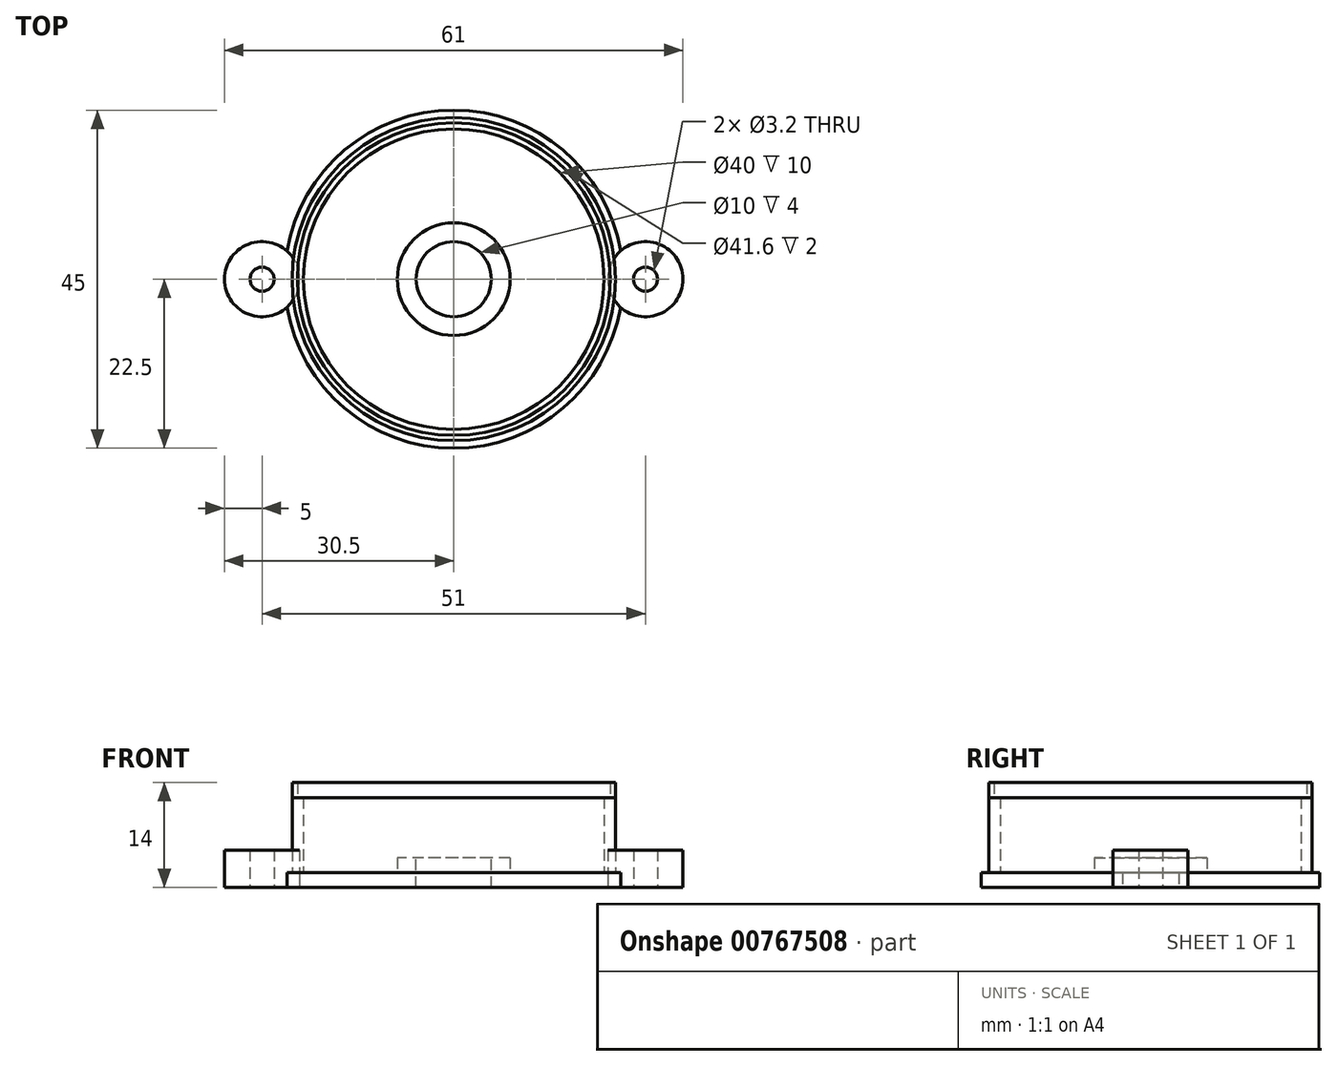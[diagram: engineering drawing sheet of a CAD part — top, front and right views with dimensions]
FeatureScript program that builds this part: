
annotation { "Feature Type Name" : "Feature", "Feature Type Description" : "" }
export const myFeature = defineFeature(function(context is Context, id is Id, definition is map)
    precondition{}
    {
        {
            var Q0;
            Q0=qCreatedBy(makeId("Top.planeOp"),FACE);
            var sketch = newSketch(context, id + "F0", { "sketchPlane" : qUnion([Q0])});
            skCircle(sketch, "E0", {"center": v(0, 0) * mm, "radius": 22.5 * mm});
            skCircle(sketch, "E1", {"center": v(25.5, 0) * mm, "radius": 5 * mm});
            skCircle(sketch, "E2", {"center": v(25.5, 0) * mm, "radius": 1.6 * mm});
            skCircle(sketch, "E3.1.0", {"center": v(-25.5, 0) * mm, "radius": 5 * mm});
            skCircle(sketch, "E3.1.1", {"center": v(-25.5, 0) * mm, "radius": 1.6 * mm});
            skSolve(sketch);
        }
        {
            var Q0;
            Q0=makeQuery(id+"F0.imprint","IMPRINT",FACE,{"disambiguationData":[TD([[makeQuery(id+"F0.imprint","IMPRINT",EDGE,{"derivedFrom":sQuery(id+"F0.wireOp",EDGE,"E3.1.1")}),-1.0]])]});
            var Q1;
            {var subQ0=sQuery(id+"F0.wireOp",EDGE,"E3.1.0");var subQ1=sQuery(id+"F0.wireOp",EDGE,"E0");var subQ2=makeQuery(id+"F0.imprint","INTERSECT",VERTEX,{"disambiguationData":[OD(0.0)],"derivedFrom":[subQ1,subQ0]});Q1=makeQuery(id+"F0.imprint","IMPRINT",FACE,{"disambiguationData":[TD([[makeQuery(id+"F0.imprint","IMPRINT",EDGE,{"disambiguationData":[TD([[subQ2,-1.0]])],"derivedFrom":subQ1}),1.0]])]});}
            var Q2;
            Q2=makeQuery(id+"F0.imprint","IMPRINT",FACE,{"disambiguationData":[TD([[makeQuery(id+"F0.imprint","IMPRINT",EDGE,{"derivedFrom":sQuery(id+"F0.wireOp",EDGE,"E2")}),-1.0]])]});
            var Q3;
            {var subQ0=sQuery(id+"F0.wireOp",EDGE,"E1");var subQ1=sQuery(id+"F0.wireOp",EDGE,"E0");var subQ2=makeQuery(id+"F0.imprint","INTERSECT",VERTEX,{"disambiguationData":[OD(0.0)],"derivedFrom":[subQ1,subQ0]});Q3=makeQuery(id+"F0.imprint","IMPRINT",FACE,{"disambiguationData":[TD([[makeQuery(id+"F0.imprint","IMPRINT",EDGE,{"disambiguationData":[TD([[subQ2,1.0]])],"derivedFrom":subQ1}),1.0]])]});}
            extrude(context, id + "F1", {"entities" : qUnion([Q0, Q1, Q2, Q3]), "depth" : 5 * mm, "offsetDistance" : 25 * mm});
        }
        {
            var Q0;
            {var subQ0=sQuery(id+"F0.wireOp",EDGE,"E3.1.0");var subQ1=sQuery(id+"F0.wireOp",EDGE,"E0");var subQ2=makeQuery(id+"F0.imprint","INTERSECT",VERTEX,{"disambiguationData":[OD(0.0)],"derivedFrom":[subQ1,subQ0]});Q0=makeQuery(id+"F0.imprint","IMPRINT",FACE,{"disambiguationData":[TD([[makeQuery(id+"F0.imprint","IMPRINT",EDGE,{"disambiguationData":[TD([[subQ2,1.0]])],"derivedFrom":subQ1}),1.0]])]});}
            extrude(context, id + "F2", {"entities" : qUnion([Q0]), "depth" : 2 * mm, "offsetDistance" : 25 * mm});
        }
        {
            var Q0;
            Q0=makeQuery(id+"F2.opExtrude","CAP_FACE",FACE,{"disambiguationData":[OSD([sQuery(id+"F0.wireOp",EDGE,"E0"),sQuery(id+"F0.wireOp",EDGE,"E1"),sQuery(id+"F0.wireOp",EDGE,"E3.1.0")])],"isStart":false});
            var sketch = newSketch(context, id + "F3", { "sketchPlane" : qUnion([Q0])});
            skCircle(sketch, "E4", {"center": v(0, 0) * mm, "radius": 20 * mm});
            skCircle(sketch, "E5", {"center": v(0, 0) * mm, "radius": 21.5 * mm});
            skSolve(sketch);
        }
        {
            var Q0;
            Q0=makeQuery(id+"F3.imprint","IMPRINT",FACE,{"disambiguationData":[TD([[makeQuery(id+"F3.imprint","IMPRINT",EDGE,{"derivedFrom":sQuery(id+"F3.wireOp",EDGE,"E4")}),-1.0]])]});
            var Q1;
            {var subQ1=makeQuery(id+"F2.opExtrude","CAP_EDGE",EDGE,{"disambiguationData":[OSD([sQuery(id+"F0.wireOp",EDGE,"E3.1.0")])],"isStart":false});Q1=makeQuery(id+"F3.imprint","IMPRINT",FACE,{"disambiguationData":[TD([[makeQuery(id+"F3.imprint","IMPRINT",EDGE,{"derivedFrom":subQ1}),1.0]])]});}
            var Q2;
            {var subQ1=makeQuery(id+"F2.opExtrude","CAP_EDGE",EDGE,{"disambiguationData":[OSD([sQuery(id+"F0.wireOp",EDGE,"E1")])],"isStart":false});Q2=makeQuery(id+"F3.imprint","IMPRINT",FACE,{"disambiguationData":[TD([[makeQuery(id+"F3.imprint","IMPRINT",EDGE,{"derivedFrom":subQ1}),1.0]])]});}
            extrude(context, id + "F4", {"entities" : qUnion([Q0, Q1, Q2]), "depth" : 10 * mm, "offsetDistance" : 25 * mm});
        }
        {
            var Q0;
            Q0=makeQuery(id+"F4.opExtrude","CAP_FACE",FACE,{"disambiguationData":[OSD([sQuery(id+"F3.wireOp",EDGE,"E4"),sQuery(id+"F3.wireOp",EDGE,"E5")])],"isStart":false});
            var sketch = newSketch(context, id + "F5", { "sketchPlane" : qUnion([Q0])});
            skCircle(sketch, "E6", {"center": v(0, 0) * mm, "radius": 20.8 * mm});
            skCircle(sketch, "E7", {"center": v(0, 0) * mm, "radius": 21.5 * mm});
            skSolve(sketch);
        }
        {
            var Q0;
            Q0=makeQuery(id+"F5.imprint","IMPRINT",FACE,{"disambiguationData":[TD([[makeQuery(id+"F5.imprint","IMPRINT",EDGE,{"derivedFrom":sQuery(id+"F5.wireOp",EDGE,"E6")}),-1.0]])]});
            extrude(context, id + "F6", {"entities" : qUnion([Q0]), "depth" : 2 * mm, "offsetDistance" : 25 * mm});
        }
        {
            var Q0;
            Q0=makeQuery(id+"FuXeZ9usWzECoiR_2.boolean.opBoolean","SPLIT",FACE,{"disambiguationData":[TD([makeQuery(id+"FuXeZ9usWzECoiR_2.opExtrude","SWEPT_FACE",FACE,{"disambiguationData":[OSD([sQuery(id+"F3.wireOp",EDGE,"E4")])]})])],"derivedFrom":makeQuery(id+"F2.opExtrude","CAP_FACE",FACE,{"disambiguationData":[OSD([sQuery(id+"F0.wireOp",EDGE,"E0"),sQuery(id+"F0.wireOp",EDGE,"E1"),sQuery(id+"F0.wireOp",EDGE,"E3.1.0")])],"isStart":false})});
            var sketch = newSketch(context, id + "F7", { "sketchPlane" : qUnion([Q0])});
            skCircle(sketch, "E8", {"center": v(0, 0) * mm, "radius": 7.5 * mm});
            skSolve(sketch);
        }
        {
            var Q0;
            Q0=makeQuery(id+"F7.imprint","IMPRINT",FACE,{"disambiguationData":[TD([[makeQuery(id+"F7.imprint","IMPRINT",EDGE,{"derivedFrom":sQuery(id+"F7.wireOp",EDGE,"E8")}),1.0]])]});
            extrude(context, id + "F8", {"entities" : qUnion([Q0]), "operationType" : NewBodyOperationType.ADD, "depth" : 2 * mm, "offsetDistance" : 25 * mm});
        }
        {
            var Q0;
            Q0=makeQuery(id+"F8.opExtrude","CAP_FACE",FACE,{"disambiguationData":[OSD([sQuery(id+"F7.wireOp",EDGE,"E8")])],"isStart":false});
            var sketch = newSketch(context, id + "F9", { "sketchPlane" : qUnion([Q0])});
            skCircle(sketch, "E9", {"center": v(0, 0) * mm, "radius": 5 * mm});
            skSolve(sketch);
        }
        {
            var Q0;
            Q0=makeQuery(id+"F9.imprint","IMPRINT",FACE,{"disambiguationData":[TD([[makeQuery(id+"F9.imprint","IMPRINT",EDGE,{"derivedFrom":sQuery(id+"F9.wireOp",EDGE,"E9")}),1.0]])]});
            extrude(context, id + "F10", {"entities" : qUnion([Q0]), "operationType" : NewBodyOperationType.REMOVE, "oppositeDirection" : true, "depth" : 5 * mm, "offsetDistance" : 25 * mm});
        }
    });
